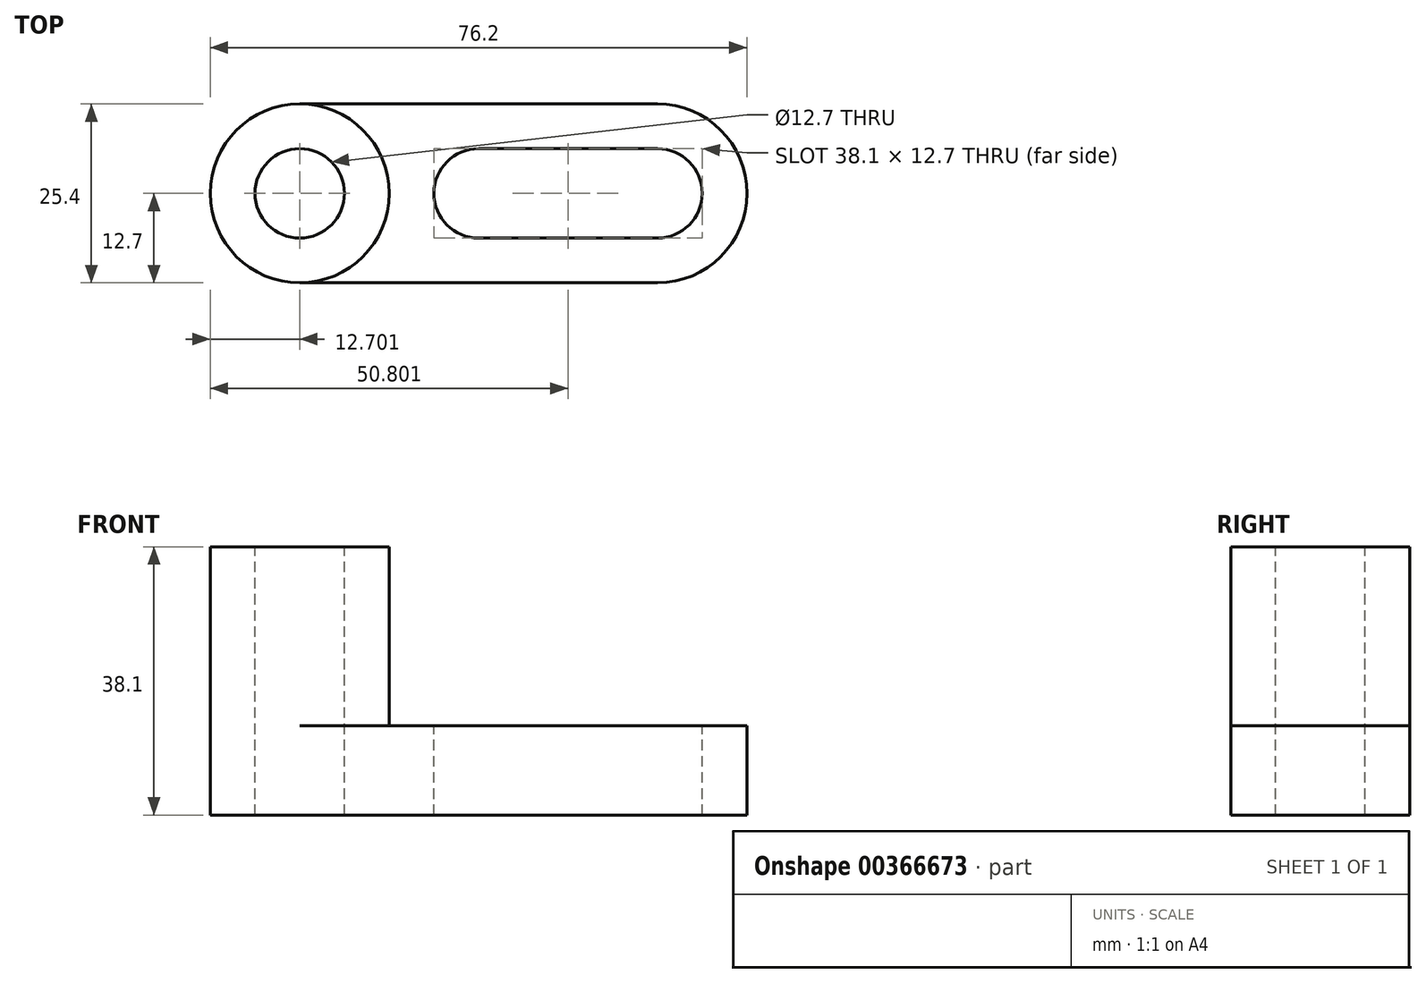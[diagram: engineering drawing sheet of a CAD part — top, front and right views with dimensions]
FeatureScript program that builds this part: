
annotation { "Feature Type Name" : "Feature", "Feature Type Description" : "" }
export const myFeature = defineFeature(function(context is Context, id is Id, definition is map)
    precondition{}
    {
        {
            var Q0;
            Q0=qCreatedBy(makeId("Front.planeOp"),FACE);
            var sketch = newSketch(context, id + "F0", { "sketchPlane" : qUnion([Q0])});
            skLineSegment(sketch, "E0", {"start": v(-76.63, 0) * mm, "end": v(-76.63, 38.1) * mm});
            skLineSegment(sketch, "E1", {"start": v(-76.63, 38.1) * mm, "end": v(-0.43, 38.1) * mm});
            skLineSegment(sketch, "E2", {"start": v(-0.43, 38.1) * mm, "end": v(-0.43, 0) * mm});
            skLineSegment(sketch, "E3", {"start": v(-0.43, 0) * mm, "end": v(-76.63, 0) * mm});
            skSolve(sketch);
        }
        {
            var Q0;
            Q0=makeQuery(id+"F0.imprint","IMPRINT",FACE,{"disambiguationData":[TD([[makeQuery(id+"F0.imprint","IMPRINT",EDGE,{"derivedFrom":sQuery(id+"F0.wireOp",EDGE,"E0")}),-1.0]])]});
            extrude(context, id + "F1", {"entities" : qUnion([Q0]), "depth" : 25.4 * mm});
        }
        {
            var Q0;
            Q0=makeQuery(id+"F1.opExtrude","CAP_FACE",FACE,{"disambiguationData":[OSD([sQuery(id+"F0.wireOp",EDGE,"E0"),sQuery(id+"F0.wireOp",EDGE,"E1"),sQuery(id+"F0.wireOp",EDGE,"E2"),sQuery(id+"F0.wireOp",EDGE,"E3")])],"isStart":false});
            var sketch = newSketch(context, id + "F2", { "sketchPlane" : qUnion([Q0])});
            skLineSegment(sketch, "E4", {"start": v(-51.23, 38.1) * mm, "end": v(-51.23, 12.7) * mm});
            skLineSegment(sketch, "E5", {"start": v(-51.23, 12.7) * mm, "end": v(-0.43, 12.7) * mm});
            skSolve(sketch);
        }
        {
            var Q0;
            {var subQ0=sQuery(id+"F2.wireOp",EDGE,"E4");Q0=makeQuery(id+"F2.imprint","IMPRINT",FACE,{"disambiguationData":[TD([[makeQuery(id+"F2.imprint","IMPRINT",EDGE,{"derivedFrom":subQ0}),1.0]])]});}
            extrude(context, id + "F3", {"entities" : qUnion([Q0]), "operationType" : NewBodyOperationType.REMOVE, "oppositeDirection" : true, "depth" : 25.4 * mm});
        }
        {
            var Q0;
            Q0=makeQuery(id+"F3.boolean.opBoolean","COPY",FACE,{"derivedFrom":makeQuery(id+"F3.opExtrude","SWEPT_FACE",FACE,{"disambiguationData":[OSD([sQuery(id+"F2.wireOp",EDGE,"E5")])]})});
            var sketch = newSketch(context, id + "F4", { "sketchPlane" : qUnion([Q0])});
            skCircle(sketch, "E6", {"center": v(-38.53, -12.7) * mm, "radius": 6.35 * mm});
            skCircle(sketch, "E7", {"center": v(-13.13, -12.7) * mm, "radius": 6.35 * mm});
            skArc(sketch, "E8", {"start": v(-13.13, -25.4) * mm, "mid": v(-0.43, -12.7) * mm, "end": v(-13.13, 0) * mm});
            skLineSegment(sketch, "E9", {"start": v(-38.53, -6.35) * mm, "end": v(-13.13, -6.35) * mm});
            skLineSegment(sketch, "E10", {"start": v(-13.13, -19.05) * mm, "end": v(-38.53, -19.05) * mm});
            skSolve(sketch);
        }
        {
            var Q0;
            {var subQ0=sQuery(id+"F4.wireOp",EDGE,"E6");var subQ1=makeQuery(id+"F4.imprint","INTERSECT",VERTEX,{"derivedFrom":[subQ0,sQuery(id+"F4.wireOp",EDGE,"E9")]});Q0=makeQuery(id+"F4.imprint","IMPRINT",FACE,{"disambiguationData":[TD([[makeQuery(id+"F4.imprint","IMPRINT",EDGE,{"disambiguationData":[TD([[subQ1,-1.0]])],"derivedFrom":subQ0}),1.0]])]});}
            var Q1;
            {var subQ0=sQuery(id+"F4.wireOp",EDGE,"E9");Q1=makeQuery(id+"F4.imprint","IMPRINT",FACE,{"disambiguationData":[TD([[makeQuery(id+"F4.imprint","IMPRINT",EDGE,{"derivedFrom":subQ0}),-1.0]])]});}
            var Q2;
            {var subQ0=sQuery(id+"F4.wireOp",EDGE,"E7");var subQ1=makeQuery(id+"F4.imprint","INTERSECT",VERTEX,{"derivedFrom":[subQ0,sQuery(id+"F4.wireOp",EDGE,"E9")]});Q2=makeQuery(id+"F4.imprint","IMPRINT",FACE,{"disambiguationData":[TD([[makeQuery(id+"F4.imprint","IMPRINT",EDGE,{"disambiguationData":[TD([[subQ1,-1.0]])],"derivedFrom":subQ0}),1.0]])]});}
            var Q3;
            {var subQ0=sQuery(id+"F4.wireOp",EDGE,"E8");var subQ1=sQuery(id+"F2.wireOp",EDGE,"E5");var subQ2=makeQuery(id+"F3.boolean.opBoolean","COPY",EDGE,{"derivedFrom":makeQuery(id+"F3.opExtrude","CAP_EDGE",EDGE,{"disambiguationData":[OSD([subQ1])],"isStart":false})});var subQ3=makeQuery(id+"F4.imprint","INTERSECT",VERTEX,{"derivedFrom":[subQ2,subQ0]});Q3=makeQuery(id+"F4.imprint","IMPRINT",FACE,{"disambiguationData":[TD([[makeQuery(id+"F4.imprint","IMPRINT",EDGE,{"disambiguationData":[TD([[subQ3,1.0]])],"derivedFrom":subQ0}),-1.0]])]});}
            var Q4;
            {var subQ0=sQuery(id+"F4.wireOp",EDGE,"E8");var subQ1=sQuery(id+"F2.wireOp",EDGE,"E5");var subQ2=makeQuery(id+"F3.boolean.opBoolean","COPY",EDGE,{"derivedFrom":makeQuery(id+"F3.opExtrude","CAP_EDGE",EDGE,{"disambiguationData":[OSD([subQ1])],"isStart":true})});var subQ3=makeQuery(id+"F4.imprint","INTERSECT",VERTEX,{"derivedFrom":[subQ2,subQ0]});Q4=makeQuery(id+"F4.imprint","IMPRINT",FACE,{"disambiguationData":[TD([[makeQuery(id+"F4.imprint","IMPRINT",EDGE,{"disambiguationData":[TD([[subQ3,-1.0]])],"derivedFrom":subQ0}),-1.0]])]});}
            extrude(context, id + "F5", {"entities" : qUnion([Q0, Q1, Q2, Q3, Q4]), "operationType" : NewBodyOperationType.REMOVE, "oppositeDirection" : true, "depth" : 25.4 * mm});
        }
        {
            var Q0;
            Q0=makeQuery(id+"F1.opExtrude","SWEPT_FACE",FACE,{"disambiguationData":[OSD([sQuery(id+"F0.wireOp",EDGE,"E1")])]});
            var sketch = newSketch(context, id + "F6", { "sketchPlane" : qUnion([Q0])});
            skCircle(sketch, "E11", {"center": v(-63.93, -12.7) * mm, "radius": 6.35 * mm});
            skCircle(sketch, "E12", {"center": v(-63.93, -12.7) * mm, "radius": 12.7 * mm});
            skSolve(sketch);
        }
        {
            var Q0;
            Q0=makeQuery(id+"F6.imprint","IMPRINT",FACE,{"disambiguationData":[TD([[makeQuery(id+"F6.imprint","IMPRINT",EDGE,{"derivedFrom":sQuery(id+"F6.wireOp",EDGE,"E11")}),1.0]])]});
            var Q1;
            {var subQ0=sQuery(id+"F6.wireOp",EDGE,"E12");var subQ1=sQuery(id+"F0.wireOp",EDGE,"E1");var subQ2=makeQuery(id+"F1.opExtrude","CAP_EDGE",EDGE,{"disambiguationData":[OSD([subQ1])],"isStart":true});var subQ3=makeQuery(id+"F6.imprint","INTERSECT",VERTEX,{"derivedFrom":[subQ2,subQ0]});Q1=makeQuery(id+"F6.imprint","IMPRINT",FACE,{"disambiguationData":[TD([[makeQuery(id+"F6.imprint","IMPRINT",EDGE,{"disambiguationData":[TD([[subQ3,-1.0]])],"derivedFrom":subQ0}),-1.0]])]});}
            var Q2;
            {var subQ0=sQuery(id+"F6.wireOp",EDGE,"E12");var subQ1=sQuery(id+"F0.wireOp",EDGE,"E1");var subQ4=makeQuery(id+"F1.opExtrude","CAP_EDGE",EDGE,{"disambiguationData":[OSD([subQ1])],"isStart":false});var subQ5=makeQuery(id+"F6.imprint","INTERSECT",VERTEX,{"derivedFrom":[subQ4,subQ0]});Q2=makeQuery(id+"F6.imprint","IMPRINT",FACE,{"disambiguationData":[TD([[makeQuery(id+"F6.imprint","IMPRINT",EDGE,{"disambiguationData":[TD([[subQ5,1.0]])],"derivedFrom":subQ0}),-1.0]])]});}
            extrude(context, id + "F7", {"entities" : qUnion([Q0, Q1, Q2]), "operationType" : NewBodyOperationType.REMOVE, "oppositeDirection" : true, "depth" : 76.2 * mm});
        }
        {
            var Q0;
            Q0=makeQuery(id+"F1.opExtrude","SWEPT_FACE",FACE,{"disambiguationData":[OSD([sQuery(id+"F0.wireOp",EDGE,"E1")])]});
            var sketch = newSketch(context, id + "F8", { "sketchPlane" : qUnion([Q0])});
            skCircle(sketch, "E13", {"center": v(-63.93, -12.7) * mm, "radius": 12.7 * mm});
            skSolve(sketch);
        }
        {
            var Q0;
            {var subQ1=sQuery(id+"F0.wireOp",EDGE,"E1");var subQ2=makeQuery(id+"F1.opExtrude","CAP_EDGE",EDGE,{"disambiguationData":[OSD([subQ1])],"isStart":true});Q0=makeQuery(id+"F8.imprint","IMPRINT",FACE,{"disambiguationData":[TD([[makeQuery(id+"F8.imprint","IMPRINT",EDGE,{"derivedFrom":subQ2}),-1.0]])]});}
            var Q1;
            {var subQ1=sQuery(id+"F0.wireOp",EDGE,"E1");var subQ2=makeQuery(id+"F1.opExtrude","CAP_EDGE",EDGE,{"disambiguationData":[OSD([subQ1])],"isStart":false});Q1=makeQuery(id+"F8.imprint","IMPRINT",FACE,{"disambiguationData":[TD([[makeQuery(id+"F8.imprint","IMPRINT",EDGE,{"derivedFrom":subQ2}),1.0]])]});}
            extrude(context, id + "F9", {"entities" : qUnion([Q0, Q1]), "operationType" : NewBodyOperationType.REMOVE, "oppositeDirection" : true, "depth" : 25.4 * mm});
        }
    });
